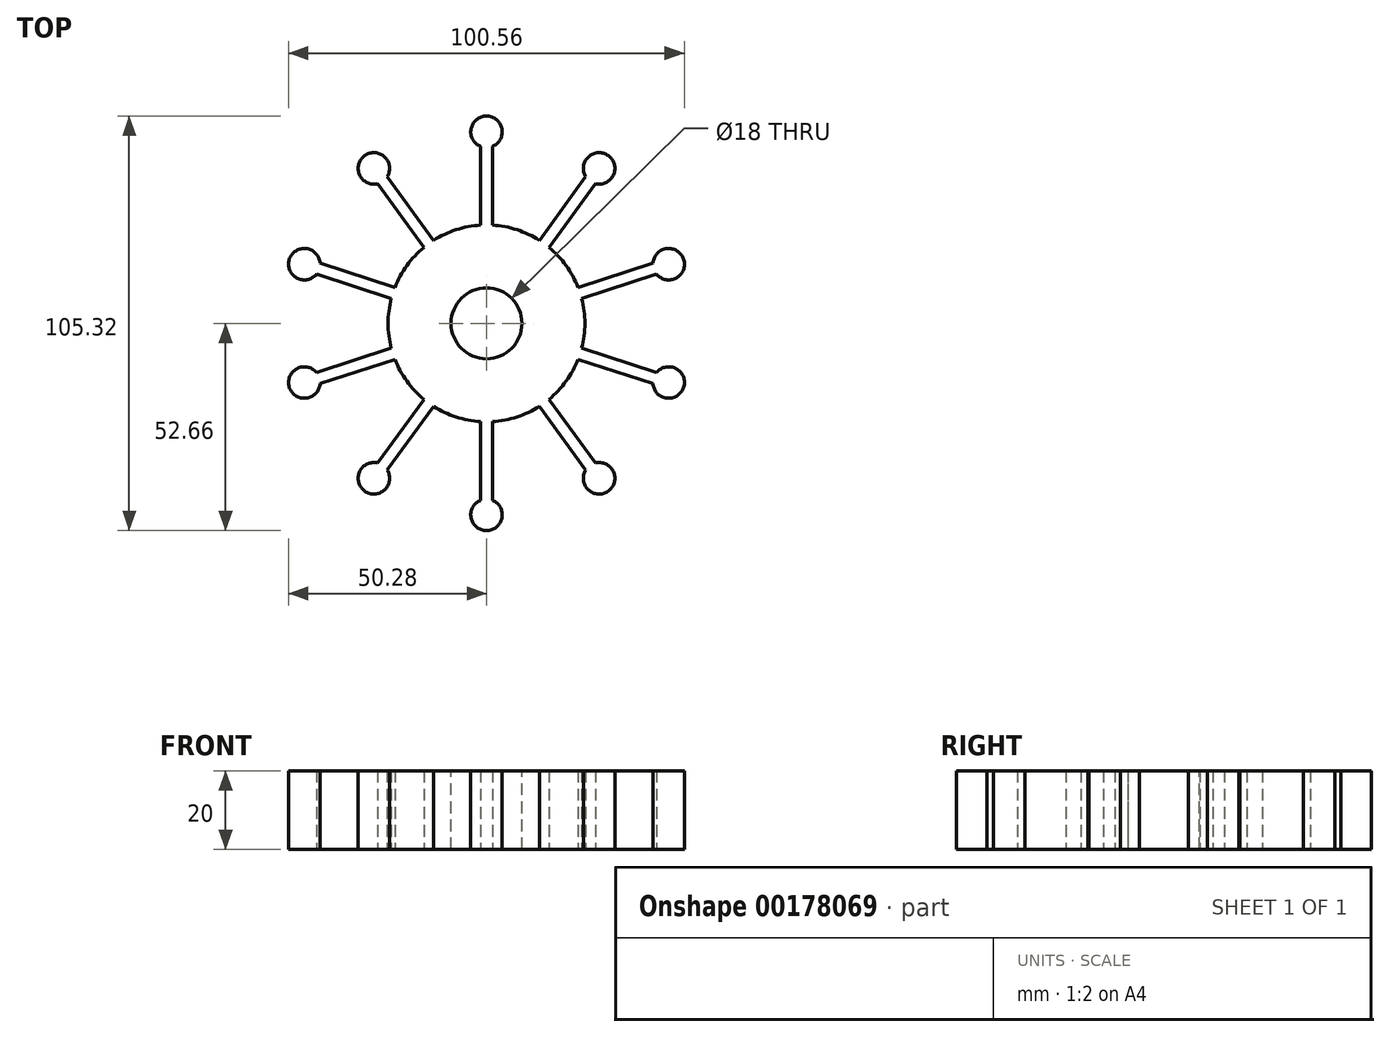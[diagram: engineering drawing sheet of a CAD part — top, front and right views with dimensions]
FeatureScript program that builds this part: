
annotation { "Feature Type Name" : "Feature", "Feature Type Description" : "" }
export const myFeature = defineFeature(function(context is Context, id is Id, definition is map)
    precondition{}
    {
        {
            var Q0;
            Q0=qCreatedBy(makeId("Top.planeOp"),FACE);
            var sketch = newSketch(context, id + "F0", { "sketchPlane" : qUnion([Q0])});
            skCircle(sketch, "E0", {"center": v(0, 0) * mm, "radius": 25 * mm});
            skLineSegment(sketch, "E1", {"start": v(0, 0) * mm, "end": v(0, 25) * mm, "construction": true});
            skCircle(sketch, "E2", {"center": v(0, 48.66) * mm, "radius": 4 * mm});
            skLineSegment(sketch, "E3", {"start": v(-1.5, 44.95) * mm, "end": v(-1.5, 24.95) * mm});
            skLineSegment(sketch, "E4.MirrorCS", {"start": v(1.5, 44.95) * mm, "end": v(1.5, 24.95) * mm});
            skCircle(sketch, "E5.1.0", {"center": v(-28.6, 39.37) * mm, "radius": 4 * mm});
            skLineSegment(sketch, "E5.1.1", {"start": v(-27.64, 35.49) * mm, "end": v(-15.88, 19.3) * mm});
            skLineSegment(sketch, "E5.1.2", {"start": v(-25.21, 37.25) * mm, "end": v(-13.45, 21.07) * mm});
            skCircle(sketch, "E5.2.0", {"center": v(-46.28, 15.04) * mm, "radius": 4 * mm});
            skLineSegment(sketch, "E5.2.1", {"start": v(-43.22, 12.47) * mm, "end": v(-24.2, 6.28) * mm});
            skLineSegment(sketch, "E5.2.2", {"start": v(-42.3, 15.32) * mm, "end": v(-23.27, 9.14) * mm});
            skCircle(sketch, "E6.1.3.0", {"center": v(-46.28, -15.04) * mm, "radius": 4 * mm});
            skLineSegment(sketch, "E6.2.3.0", {"start": v(-42.3, -15.32) * mm, "end": v(-23.27, -9.14) * mm});
            skLineSegment(sketch, "E6.5.3.0", {"start": v(-43.22, -12.47) * mm, "end": v(-24.2, -6.28) * mm});
            skCircle(sketch, "E6.1.4.0", {"center": v(-28.6, -39.37) * mm, "radius": 4 * mm});
            skLineSegment(sketch, "E6.2.4.0", {"start": v(-25.21, -37.25) * mm, "end": v(-13.45, -21.07) * mm});
            skLineSegment(sketch, "E6.5.4.0", {"start": v(-27.64, -35.49) * mm, "end": v(-15.88, -19.3) * mm});
            skCircle(sketch, "E6.1.5.0", {"center": v(0, -48.66) * mm, "radius": 4 * mm});
            skLineSegment(sketch, "E6.2.5.0", {"start": v(1.5, -44.95) * mm, "end": v(1.5, -24.95) * mm});
            skLineSegment(sketch, "E6.5.5.0", {"start": v(-1.5, -44.95) * mm, "end": v(-1.5, -24.95) * mm});
            skCircle(sketch, "E6.1.6.0", {"center": v(28.6, -39.37) * mm, "radius": 4 * mm});
            skLineSegment(sketch, "E6.2.6.0", {"start": v(27.64, -35.49) * mm, "end": v(15.88, -19.3) * mm});
            skLineSegment(sketch, "E6.5.6.0", {"start": v(25.21, -37.25) * mm, "end": v(13.45, -21.07) * mm});
            skCircle(sketch, "E6.1.7.0", {"center": v(46.28, -15.04) * mm, "radius": 4 * mm});
            skLineSegment(sketch, "E6.2.7.0", {"start": v(43.22, -12.47) * mm, "end": v(24.2, -6.28) * mm});
            skLineSegment(sketch, "E6.5.7.0", {"start": v(42.3, -15.32) * mm, "end": v(23.27, -9.14) * mm});
            skCircle(sketch, "E6.1.8.0", {"center": v(46.28, 15.04) * mm, "radius": 4 * mm});
            skLineSegment(sketch, "E6.2.8.0", {"start": v(42.3, 15.32) * mm, "end": v(23.27, 9.14) * mm});
            skLineSegment(sketch, "E6.5.8.0", {"start": v(43.22, 12.47) * mm, "end": v(24.2, 6.28) * mm});
            skCircle(sketch, "E6.1.9.0", {"center": v(28.6, 39.37) * mm, "radius": 4 * mm});
            skLineSegment(sketch, "E6.2.9.0", {"start": v(25.21, 37.25) * mm, "end": v(13.45, 21.07) * mm});
            skLineSegment(sketch, "E6.5.9.0", {"start": v(27.64, 35.49) * mm, "end": v(15.88, 19.3) * mm});
            skSolve(sketch);
        }
        {
            var Q0;
            Q0 = qSketchRegion(id + "F0", true);
            extrude(context, id + "F1", {"entities" : qUnion([Q0]), "depth" : 20 * mm});
        }
        {
            var Q0;
            Q0=makeQuery(id+"F1.opExtrude","CAP_FACE",FACE,{"disambiguationData":[OSD([sQuery(id+"F0.wireOp",EDGE,"E0"),sQuery(id+"F0.wireOp",EDGE,"E2"),sQuery(id+"F0.wireOp",EDGE,"E3"),sQuery(id+"F0.wireOp",EDGE,"E4.MirrorCS"),sQuery(id+"F0.wireOp",EDGE,"E5.1.0"),sQuery(id+"F0.wireOp",EDGE,"E5.1.1"),sQuery(id+"F0.wireOp",EDGE,"E5.1.2"),sQuery(id+"F0.wireOp",EDGE,"E5.2.0"),sQuery(id+"F0.wireOp",EDGE,"E5.2.1"),sQuery(id+"F0.wireOp",EDGE,"E5.2.2"),sQuery(id+"F0.wireOp",EDGE,"E6.1.3.0"),sQuery(id+"F0.wireOp",EDGE,"E6.2.3.0"),sQuery(id+"F0.wireOp",EDGE,"E6.5.3.0"),sQuery(id+"F0.wireOp",EDGE,"E6.1.4.0"),sQuery(id+"F0.wireOp",EDGE,"E6.2.4.0"),sQuery(id+"F0.wireOp",EDGE,"E6.5.4.0"),sQuery(id+"F0.wireOp",EDGE,"E6.1.5.0"),sQuery(id+"F0.wireOp",EDGE,"E6.2.5.0"),sQuery(id+"F0.wireOp",EDGE,"E6.5.5.0"),sQuery(id+"F0.wireOp",EDGE,"E6.1.6.0"),sQuery(id+"F0.wireOp",EDGE,"E6.2.6.0"),sQuery(id+"F0.wireOp",EDGE,"E6.5.6.0"),sQuery(id+"F0.wireOp",EDGE,"E6.1.7.0"),sQuery(id+"F0.wireOp",EDGE,"E6.2.7.0"),sQuery(id+"F0.wireOp",EDGE,"E6.5.7.0"),sQuery(id+"F0.wireOp",EDGE,"E6.1.8.0"),sQuery(id+"F0.wireOp",EDGE,"E6.2.8.0"),sQuery(id+"F0.wireOp",EDGE,"E6.5.8.0"),sQuery(id+"F0.wireOp",EDGE,"E6.1.9.0"),sQuery(id+"F0.wireOp",EDGE,"E6.2.9.0"),sQuery(id+"F0.wireOp",EDGE,"E6.5.9.0")])],"isStart":false});
            var sketch = newSketch(context, id + "F2", { "sketchPlane" : qUnion([Q0])});
            skCircle(sketch, "E7", {"center": v(0, 0) * mm, "radius": 9 * mm});
            skSolve(sketch);
        }
        {
            var Q0;
            Q0 = qSketchRegion(id + "F2", true);
            extrude(context, id + "F3", {"entities" : qUnion([Q0]), "operationType" : NewBodyOperationType.REMOVE, "endBound" : BoundingType.THROUGH_ALL, "oppositeDirection" : true, "depth" : 25 * mm});
        }
    });
